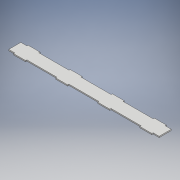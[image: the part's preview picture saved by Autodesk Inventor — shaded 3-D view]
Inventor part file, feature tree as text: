
AUTODESK INVENTOR PART (.ipt)
format: ipt  version: 2018 (Build 220112000, 112)  size: 135,168 bytes
history: native  units: mm
features: extrude x1, sketch x1
ambient origin geometry x8: Origin, YZ Plane, XZ Plane, XY Plane, X Axis, Y Axis, Z Axis, Center Point
bodies: Solid1 (feature_tree)
feature tree (2):
  extrude  "Extrusion1"  Depth=40.0mm
  sketch  "Sketch1"  dims[d0=40.0mm d1=40.0mm d2=40.0mm d3=40.0mm d4=40.0mm d5=498.0mm d6=40.0mm d7=4.0mm d8=0.0mm]
